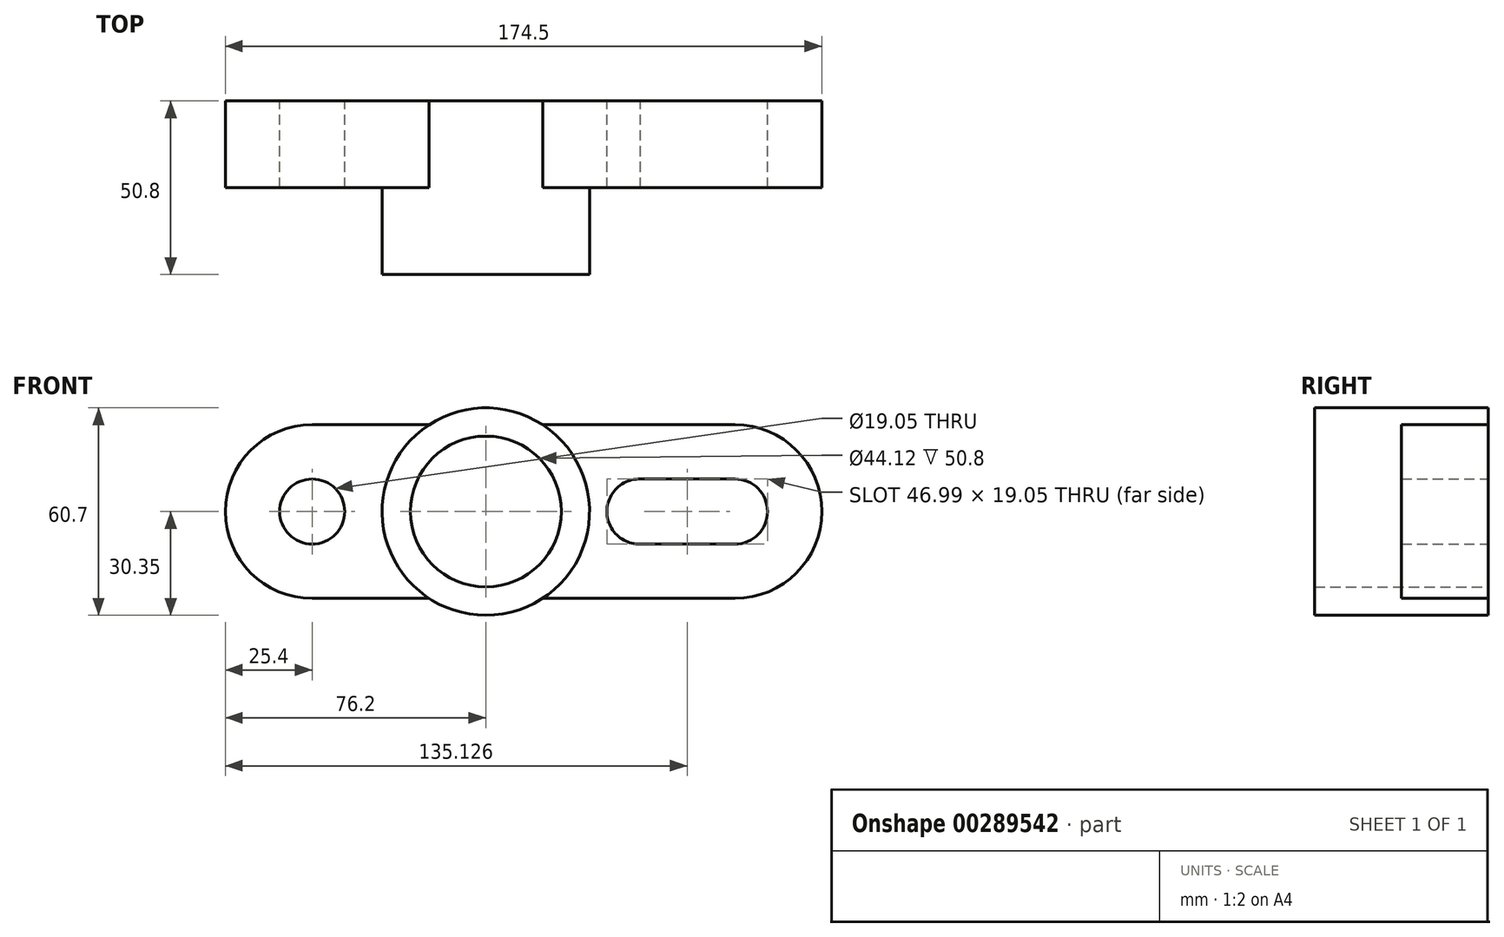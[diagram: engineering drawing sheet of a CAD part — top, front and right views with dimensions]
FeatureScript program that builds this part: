
annotation { "Feature Type Name" : "Feature", "Feature Type Description" : "" }
export const myFeature = defineFeature(function(context is Context, id is Id, definition is map)
    precondition{}
    {
        {
            var Q0;
            Q0=qCreatedBy(makeId("Front.planeOp"),FACE);
            var sketch = newSketch(context, id + "F0", { "sketchPlane" : qUnion([Q0])});
            skCircle(sketch, "E0", {"center": v(0, 0) * mm, "radius": 30.35 * mm});
            skLineSegment(sketch, "E1", {"start": v(16.62, -25.4) * mm, "end": v(72.9, -25.4) * mm});
            skLineSegment(sketch, "E2", {"start": v(16.62, 25.4) * mm, "end": v(72.9, 25.4) * mm});
            skLineSegment(sketch, "E3", {"start": v(-16.62, -25.4) * mm, "end": v(-50.8, -25.4) * mm});
            skLineSegment(sketch, "E4", {"start": v(-16.62, 25.4) * mm, "end": v(-50.8, 25.4) * mm});
            skArc(sketch, "E5", {"start": v(-50.8, 25.4) * mm, "mid": v(-76.2, 0) * mm, "end": v(-50.8, -25.4) * mm});
            skArc(sketch, "E6", {"start": v(72.9, -25.4) * mm, "mid": v(98.3, 0) * mm, "end": v(72.9, 25.4) * mm});
            skCircle(sketch, "E7", {"center": v(-50.8, 0) * mm, "radius": 9.53 * mm});
            skArc(sketch, "E8", {"start": v(72.9, 9.53) * mm, "mid": v(82.42, 0) * mm, "end": v(72.9, -9.53) * mm});
            skArc(sketch, "E9", {"start": v(45.24, 9.52) * mm, "mid": v(35.43, 0) * mm, "end": v(45.24, -9.53) * mm});
            skLineSegment(sketch, "E10", {"start": v(72.9, 9.53) * mm, "end": v(45.24, 9.52) * mm});
            skLineSegment(sketch, "E11", {"start": v(72.9, -9.52) * mm, "end": v(45.24, -9.53) * mm});
            skCircle(sketch, "E12", {"center": v(0, 0) * mm, "radius": 22.06 * mm});
            skCircle(sketch, "E13", {"center": v(0, 0) * mm, "radius": 14.02 * mm});
            skCircle(sketch, "E14", {"center": v(0, 0) * mm, "radius": 30.28 * mm});
            skSolve(sketch);
        }
        {
            var Q0;
            Q0=makeQuery(id+"F0.imprint","IMPRINT",FACE,{"disambiguationData":[TD([[makeQuery(id+"F0.imprint","IMPRINT",EDGE,{"derivedFrom":sQuery(id+"F0.wireOp",EDGE,"E14")}),-1.0]])]});
            var Q1;
            Q1=makeQuery(id+"F0.imprint","IMPRINT",FACE,{"disambiguationData":[TD([[makeQuery(id+"F0.imprint","IMPRINT",EDGE,{"derivedFrom":sQuery(id+"F0.wireOp",EDGE,"E12")}),-1.0]])]});
            var Q2;
            {var subQ1=sQuery(id+"F0.wireOp",EDGE,"E3");Q2=makeQuery(id+"F0.imprint","IMPRINT",FACE,{"disambiguationData":[TD([[makeQuery(id+"F0.imprint","IMPRINT",EDGE,{"derivedFrom":subQ1}),-1.0]])]});}
            var Q3;
            {var subQ1=sQuery(id+"F0.wireOp",EDGE,"E1");Q3=makeQuery(id+"F0.imprint","IMPRINT",FACE,{"disambiguationData":[TD([[makeQuery(id+"F0.imprint","IMPRINT",EDGE,{"derivedFrom":subQ1}),1.0]])]});}
            extrude(context, id + "F1", {"entities" : qUnion([Q0, Q1, Q2, Q3]), "depth" : 25.4 * mm});
        }
        {
            var Q0;
            Q0=makeQuery(id+"F1.opExtrude","CAP_FACE",FACE,{"disambiguationData":[OSD([sQuery(id+"F0.wireOp",EDGE,"E0"),sQuery(id+"F0.wireOp",EDGE,"E1"),sQuery(id+"F0.wireOp",EDGE,"E2"),sQuery(id+"F0.wireOp",EDGE,"E3"),sQuery(id+"F0.wireOp",EDGE,"E4"),sQuery(id+"F0.wireOp",EDGE,"E5"),sQuery(id+"F0.wireOp",EDGE,"E6"),sQuery(id+"F0.wireOp",EDGE,"E7"),sQuery(id+"F0.wireOp",EDGE,"E8"),sQuery(id+"F0.wireOp",EDGE,"E9"),sQuery(id+"F0.wireOp",EDGE,"E10"),sQuery(id+"F0.wireOp",EDGE,"E11"),sQuery(id+"F0.wireOp",EDGE,"E12")])],"isStart":false});
            var sketch = newSketch(context, id + "F2", { "sketchPlane" : qUnion([Q0])});
            skCircle(sketch, "E15", {"center": v(0, 0) * mm, "radius": 30.34 * mm});
            skCircle(sketch, "E16", {"center": v(0, 0) * mm, "radius": 21.94 * mm});
            skSolve(sketch);
        }
        {
            var Q0;
            Q0=makeQuery(id+"F2.imprint","IMPRINT",FACE,{"disambiguationData":[TD([[makeQuery(id+"F2.imprint","IMPRINT",EDGE,{"derivedFrom":sQuery(id+"F2.wireOp",EDGE,"E15")}),1.0]])]});
            extrude(context, id + "F3", {"entities" : qUnion([Q0]), "operationType" : NewBodyOperationType.ADD, "depth" : 25.4 * mm});
        }
    });
